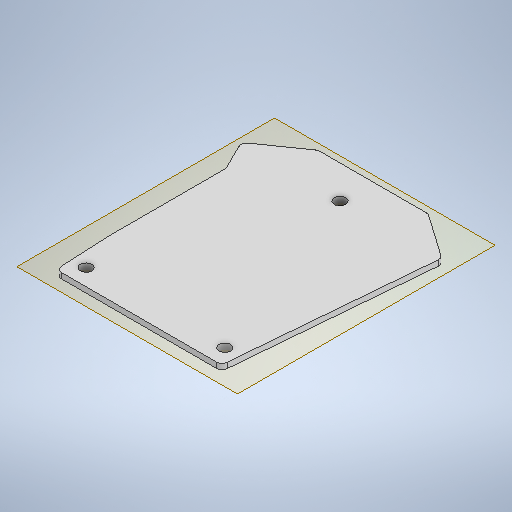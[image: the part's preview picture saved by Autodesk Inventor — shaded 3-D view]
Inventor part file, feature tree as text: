
AUTODESK INVENTOR PART (.ipt)
format: ipt  version: 2025.1 (Build 291241000, 241)  size: 295,936 bytes
history: native  units: mm
features: reference x5, sketch x4, other x3, extrude x2, plane x1, hole x1, fillet x1
ambient origin geometry x8: Origin, YZ Plane, XZ Plane, XY Plane, X Axis, Y Axis, Z Axis, Center Point
bodies: Volumenkörper1 (feature_tree)
feature tree (17):
  plane  "Arbeitsebene1"
  extrude  "Extrusion1"  Depth=2.0mm
  sketch  "Skizze2"  dims[d3=2.0mm d4=0.0mm]
  extrude  "Extrusion2"  Depth=2.0mm
  hole  "Bohrung1"  [1 undecoded]
  fillet  "Rundung1"  [1 undecoded]
  sketch  "Skizze1"  dims[d0=2.0mm d1=0.0mm d2=0.5mm]
  reference  "Referenz1"
  sketch  "Skizze3"  dims[d5=4.2mm d6=6.0mm d7=4.0mm d8=2.0mm d9=90.0deg d10=8.0mm d11=20.594885mm d12=2.0mm]
  reference  "Referenz2"
  sketch  "Skizze4"
  reference  "Referenz3"
  reference  "Referenz4"
  reference  "Referenz5"
  other  "<userpath>\OneDrive\Documents\Projekte\Macrolampe\CAD\Baugruppen\Macrolight.iam"
  other  "Macrolight.iam"
  other  "Gehaueseunterteil:1"
note: 2 required parameter values undecoded (feature->parameter linkage not recoverable at this tier; creation-order binding heuristic only, values carry confidence <= 0.55)
